# Revit family: Clevertronics_LLIFE-RECSP
name_source: partatom
category: Lighting Fixtures
units: mm (PartAtom-declared; Revit-internal decimal feet)

## family parameters
Cut with Voids When Loaded = No
Host = Face
Light Source = Yes
Part Type = Normal
Room Calculation Point = No
Round Connector Dimension = Use Diameter
Shared = No

## types (8) — shared parameters
Apparent Load = 5 VA
Clevertronics_AS2293 Classification = C0=D50 C90=D50
Clevertronics_Applicable Standards = AS/NZS3820, CISPR15, AS/NZS2293.3
Clevertronics_Battery = 3.3V 2500mAh
Clevertronics_Battery Type = Lithium Nanophosphate
Clevertronics_Ceiling Hole Cut-Out = 80mm
Clevertronics_Charger Method = Intelligent current limited constant voltage
Clevertronics_Construction = PC/ABS head
Clevertronics_Dimensions Main Enclosure = 232mm x 51mm x 42mm (Control pack)_95mm Head diameter
Clevertronics_Height = 42 mm  [stored 0.137795 ft]
Clevertronics_IP Rating = IP44 (parts below ceiling) IP20 (parts above ceiling)
Clevertronics_Length = 232 mm  [stored 0.761155 ft]
Clevertronics_Material = Clevertronics_Plycarbonate Base
Clevertronics_Minimum Ceiling Depth = 120mm
Clevertronics_Mounting = Recessed Ceiling
Clevertronics_Operating Mode = Non-maintained
Clevertronics_Operating Temperature = 1˚C to 40˚C
Clevertronics_Operating Voltage = 240V AC; 50Hz
Clevertronics_Replacement Battery = 1530010
Clevertronics_Width = 51 mm
Color Filter = 16777215
Default Elevation = 1200 mm
Dimming Lamp Color Temperature Shift = <None>
Lamp = Single LED (Lifetime warranty on the lamp head and loom assembly)
Manufacturer = Clevertronics
Photometric Web File = LLIFE-RECSP-HV_AUD01820020001_IESA_E_LL24373A_202211301210.ies
Tilt Angle = -90.00°
zero-valued in all types: Clevertronics_Annotation Size

## per-type parameters (varying)
| type | Clevertronics_Emergency Driver | Clevertronics_Emergency Lamp | Clevertronics_MIC Number | Clevertronics_Power Consumption | Clevertronics_Product Description | Clevertronics_Testing Node | Clevertronics_Testing System | Clevertronics_Weight | Description | Model |
| LLIFE-RECSP-ZW_AUD01120020001 | AUM01170040001 LLIFE-CKIT-ZW | 8050260 | AUD01120020001 | 1.3 Watts (Standby), 4.5 Watts (Max) | L10 Optimum Lifelight, Recessed Emergency Light with IP44 Splash Proof Head | 8001450 | Zoneworks Computerised Testing |  | L10 Optimum Lifelight, Recessed Emergency Light with IP44 Splash Proof Head | LLIFE-RECSP-ZW |
| LLIFE-RECSP_AUD01320020001 | AUM01370030002
LLIFE-CKIT
AUM01370030002
LLIFE-CKIT
AUM01370030002
LLIFE-CKIT
AUM01370030002 LLIFE-CKIT | 1100760 | AUD01320020001 | 1.0 Watts (Standby), 4.2 Watts (Max) | L10 Optimum Lifelight, High Performance, Recessed Emergency Light with IP44 Splash Proof Head, Enabled with Clevertest Plus
IP44 Splash Proof Head, Enabled with Clevertest Plus
L10 Optimum Lifelight, High Performance, Recessed Emergency Light with
IP44 Splash Proof Head, Enabled with Clevertest Plus
L10 Optimum Lifelight, High Performance, Recessed Emergency Light with IP44 Splash Proof Head, Enabled with Clevertest Plus |  | Clevertest Plus Enabled (Not activated by default) |  | L10 Optimum Lifelight, High Performance, Recessed Emergency Light with IP44 Splash Proof Head, Enabled with Clevertest Plus
IP44 Splash Proof Head, Enabled with Clevertest Plus
L10 Optimum Lifelight, High Performance, Recessed Emergency Light with
IP44 Splash Proof Head, Enabled with Clevertest Plus
L10 Optimum Lifelight, High Performance, Recessed Emergency Light with IP44 Splash Proof Head, Enabled with Clevertest Plus | LLIFE-RECSP |
| LLIFE-RECSP-BLK_AUD01320030001 | AUM01370030002
LLIFE-CKIT
AUM01370030002
LLIFE-CKIT
AUM01370030002
LLIFE-CKIT
AUM01370030002 LLIFE-CKIT | 1100762 | AUD01320030001 | 1.0 Watts (Standby), 4.2 Watts (Max) | L10 Optimum Lifelight, High Performance, Recessed Emergency Light with IP44 Splash Proof Head, Black, Enabled with Clevertest Plus
IP44 Splash Proof Head, Enabled with Clevertest Plus
L10 Optimum Lifelight, High Performance, Recessed Emergency Light with
L10 Optimum Lifelight, High Performance, Recessed Emergency Light with IP44 Splash Proof Head, Enabled with Clevertest Plus
L10 Optimum Lifelight, High Performance, Recessed Emergency Light with IP44 Splash Proof Head, Enabled with Clevertest Plus |  | Clevertest Plus Enabled (Not activated by default) |  | L10 Optimum Lifelight, High Performance, Recessed Emergency Light with IP44 Splash Proof Head, Black, Enabled with Clevertest Plus
IP44 Splash Proof Head, Enabled with Clevertest Plus
L10 Optimum Lifelight, High Performance, Recessed Emergency Light with
L10 Optimum Lifelight, High Performance, Recessed Emergency Light with IP44 Splash Proof Head, Enabled with Clevertest Plus
L10 Optimum Lifelight, High Performance, Recessed Emergency Light with IP44 Splash Proof Head, Enabled with Clevertest Plus | LLIFE-RECSP-BLK |
| LLIFE-RECSP-DALI_AUD01220020002 | AUM01270310002
LLIFE-CKIT
AUM01370030002
LLIFE-CKIT
AUM01370030002
LLIFE-CKIT
AUM01370030002 LLIFE-CKIT | 1100760 | AUD01220020002 | 1.3 Watts (Standby), 4.5 Watts (Max) | Lifelight IP44 Splashproof Emergency, Recessed Mount, L10 Nanophosphate, DALI Emergency | 8003060 | DALI Registered | 0.8 | Lifelight IP44 Splashproof Emergency, Recessed Mount, L10 Nanophosphate, DALI Emergency | LLIFE-RECSP-DALI |
| LLIFE-RECSP-DALI-BLK_AUD01210110002 | AUM01270310002
LLIFE-CKIT
AUM01370030002
LLIFE-CKIT
AUM01370030002
LLIFE-CKIT
AUM01370030002 LLIFE-CKIT | 1100762 | AUD01210110002 | 1.3 Watts (Standby), 4.5 Watts (Max) | Lifelight IP44 Splashproof Emergency, Recessed Mount, L10 Nanophosphate, DALI Emergency, Black | 8003060 | DALI Registered | 0.8 | Lifelight IP44 Splashproof Emergency, Recessed Mount, L10 Nanophosphate, DALI Emergency, Black | LLIFE-RECSP-DALI-BLK |
| LLIFE-RECSP-HV_AUD01820020001 | AUM01870020001
LLIFE-CKIT
AUM01370030002
LLIFE-CKIT
AUM01370030002
LLIFE-CKIT
AUM01370030002 LLIFE-CKIT | 1100760 | AUD01820020001 | 1.3 Watts (Standby), 4.5 Watts (Max) | Lifelight IP44 Splashproof Emergency, Recessed Mount, L10 Nanophosphate, Zoneworks XT Hive | 8003190 | Zoneworks XT HIVE (RF) |  | Lifelight IP44 Splashproof Emergency, Recessed Mount, L10 Nanophosphate, Zoneworks XT Hive | LLIFE-RECSP-HV |
| LLIFE-RECSP-HV-BLK_AUD01820060001 | AUM01870020001
LLIFE-CKIT
AUM01370030002
LLIFE-CKIT
AUM01370030002
LLIFE-CKIT
AUM01370030002 LLIFE-CKIT | 1100762 | AUD01820060001 | 1.3 Watts (Standby), 4.5 Watts (Max) | Lifelight IP44 Splashproof Emergency, Recessed Mount, L10 Nanophosphate, Zoneworks XT Hive, Black | 8003190 | Zoneworks XT HIVE (RF) |  | Lifelight IP44 Splashproof Emergency, Recessed Mount, L10 Nanophosphate, Zoneworks XT Hive, Black | LLIFE-RECSP-HV-BLK |
| LLIFE-RECSP-HVG_AUD01920030001 | AUM01970100001
LLIFE-CKIT
AUM01370030002
LLIFE-CKIT
AUM01370030002
LLIFE-CKIT
AUM01370030002 LLIFE-CKIT | 1100760 | AUD01920030001 | 1.3 Watts (Standby), 4.5 Watts (Max) | Lifelight IP44 Splashproof Emergency, Recessed Mount, L10 Nanophosphate, 
Zoneworks XT Hive
Lifelight IP44 Splashproof Emergency, Recessed Mount, L10 Nanophosphate, 
Zoneworks XT Hive
Lifelight IP44 Splashproof Emergency, Recessed Mount, L10 Nanophosphate, Zoneworks XT Hive | 8003560 | Zoneworks XT HIVE (RF) 2.4GHz |  | Lifelight IP44 Splashproof Emergency, Recessed Mount, L10 Nanophosphate, Zoneworks XT Hive | LLIFE-RECSP-HVG |

note: [stored X ft] marks values corroborated as IEEE doubles in the binary element streams (Revit-internal decimal feet)

## geometry (parser evidence)
native form markers: Blend x4, Sweep x3
no freeform markers — native parametric forms only
